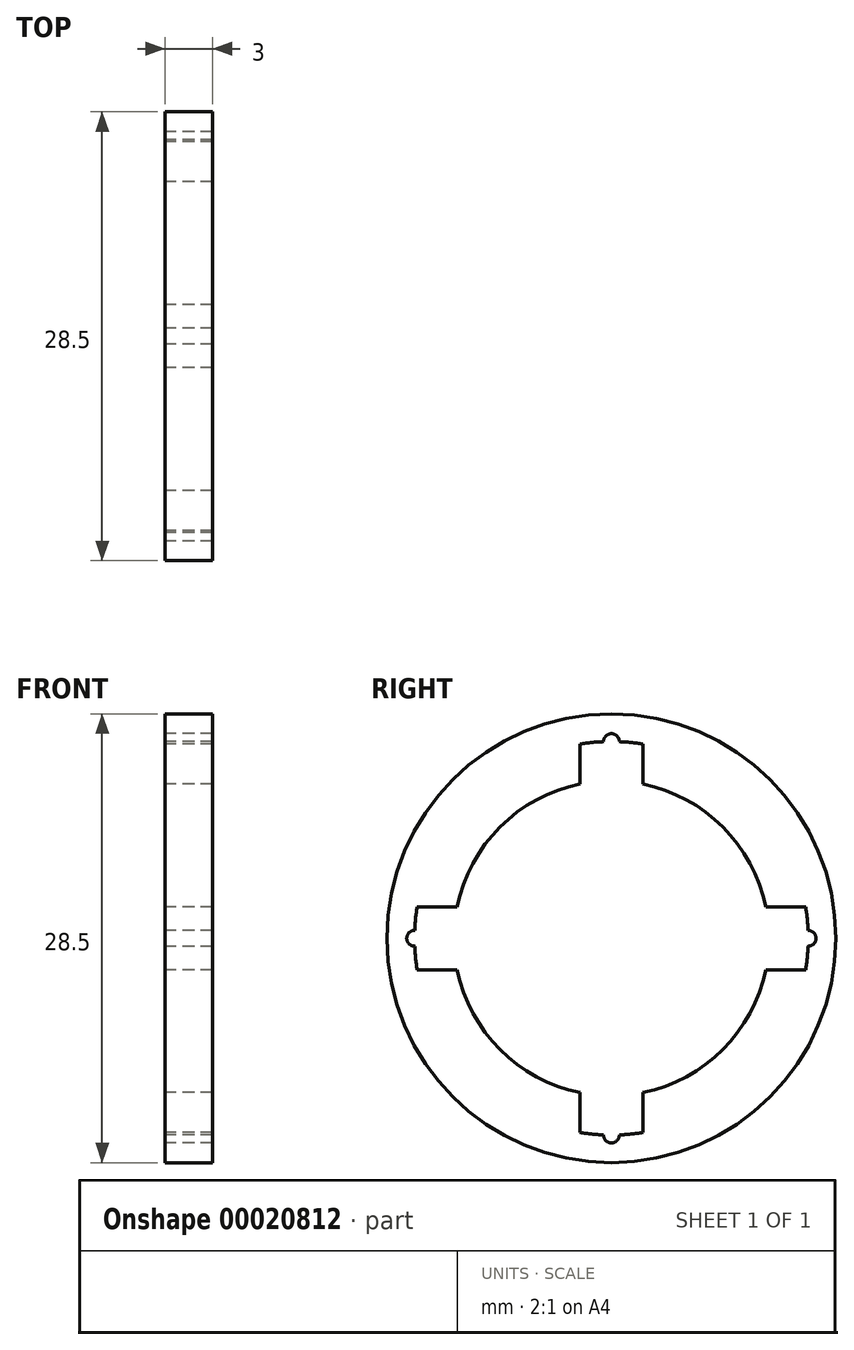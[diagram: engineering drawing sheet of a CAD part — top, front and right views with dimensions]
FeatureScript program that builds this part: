
annotation { "Feature Type Name" : "Feature", "Feature Type Description" : "" }
export const myFeature = defineFeature(function(context is Context, id is Id, definition is map)
    precondition{}
    {
        {
            var Q0;
            Q0=qCreatedBy(makeId("Right.planeOp"),FACE);
            var sketch = newSketch(context, id + "F0", { "sketchPlane" : qUnion([Q0])});
            skCircle(sketch, "E0", {"center": v(0, 0) * mm, "radius": 10 * mm});
            skCircle(sketch, "E1", {"center": v(0, 0) * mm, "radius": 12.5 * mm});
            skCircle(sketch, "E2", {"center": v(0, 0) * mm, "radius": 14.25 * mm});
            skLineSegment(sketch, "E3.rect.bottom", {"start": v(-12.34, 2) * mm, "end": v(12.34, 2) * mm});
            skLineSegment(sketch, "E3.rect.top", {"start": v(-12.34, -2) * mm, "end": v(12.34, -2) * mm});
            skLineSegment(sketch, "E3.rect.left", {"start": v(-12.34, 2) * mm, "end": v(-12.34, -2) * mm});
            skLineSegment(sketch, "E3.rect.right", {"start": v(12.34, 2) * mm, "end": v(12.34, -2) * mm});
            skLineSegment(sketch, "E4.rect.bottom", {"start": v(-2, 12.34) * mm, "end": v(2, 12.34) * mm});
            skLineSegment(sketch, "E4.rect.top", {"start": v(-2, -12.34) * mm, "end": v(2, -12.34) * mm});
            skLineSegment(sketch, "E4.rect.left", {"start": v(-2, 12.34) * mm, "end": v(-2, -12.34) * mm});
            skLineSegment(sketch, "E4.rect.right", {"start": v(2, 12.34) * mm, "end": v(2, -12.34) * mm});
            skCircle(sketch, "E5", {"center": v(-12.5, 0) * mm, "radius": 0.5 * mm});
            skCircle(sketch, "E6", {"center": v(12.5, 0) * mm, "radius": 0.5 * mm});
            skCircle(sketch, "E7", {"center": v(0, 12.5) * mm, "radius": 0.5 * mm});
            skCircle(sketch, "E8", {"center": v(0, -12.5) * mm, "radius": 0.5 * mm});
            skSolve(sketch);
        }
        {
            var Q0;
            Q0=makeQuery(id+"F0.imprint","IMPRINT",FACE,{"disambiguationData":[TD([[makeQuery(id+"F0.imprint","IMPRINT",EDGE,{"derivedFrom":sQuery(id+"F0.wireOp",EDGE,"E2")}),1.0]])]});
            var Q1;
            {var subQ0=sQuery(id+"F0.wireOp",EDGE,"E4.rect.left");var subQ1=sQuery(id+"F0.wireOp",EDGE,"E0");var subQ2=makeQuery(id+"F0.imprint","INTERSECT",VERTEX,{"disambiguationData":[OD(0.0)],"derivedFrom":[subQ1,subQ0]});Q1=makeQuery(id+"F0.imprint","IMPRINT",FACE,{"disambiguationData":[TD([[makeQuery(id+"F0.imprint","IMPRINT",EDGE,{"disambiguationData":[TD([[subQ2,-1.0]])],"derivedFrom":subQ1}),-1.0]])]});}
            var Q2;
            {var subQ1=sQuery(id+"F0.wireOp",EDGE,"E0");var subQ5=sQuery(id+"F0.wireOp",EDGE,"E3.rect.top");var subQ6=makeQuery(id+"F0.imprint","INTERSECT",VERTEX,{"disambiguationData":[OD(0.0)],"derivedFrom":[subQ1,subQ5]});Q2=makeQuery(id+"F0.imprint","IMPRINT",FACE,{"disambiguationData":[TD([[makeQuery(id+"F0.imprint","IMPRINT",EDGE,{"disambiguationData":[TD([[subQ6,-1.0]])],"derivedFrom":subQ1}),-1.0]])]});}
            var Q3;
            {var subQ0=sQuery(id+"F0.wireOp",EDGE,"E4.rect.right");var subQ1=sQuery(id+"F0.wireOp",EDGE,"E0");var subQ2=makeQuery(id+"F0.imprint","INTERSECT",VERTEX,{"disambiguationData":[OD(1.0)],"derivedFrom":[subQ1,subQ0]});Q3=makeQuery(id+"F0.imprint","IMPRINT",FACE,{"disambiguationData":[TD([[makeQuery(id+"F0.imprint","IMPRINT",EDGE,{"disambiguationData":[TD([[subQ2,-1.0]])],"derivedFrom":subQ1}),-1.0]])]});}
            var Q4;
            {var subQ0=sQuery(id+"F0.wireOp",EDGE,"E4.rect.right");var subQ1=sQuery(id+"F0.wireOp",EDGE,"E0");var subQ2=makeQuery(id+"F0.imprint","INTERSECT",VERTEX,{"disambiguationData":[OD(0.0)],"derivedFrom":[subQ1,subQ0]});Q4=makeQuery(id+"F0.imprint","IMPRINT",FACE,{"disambiguationData":[TD([[makeQuery(id+"F0.imprint","IMPRINT",EDGE,{"disambiguationData":[TD([[subQ2,1.0]])],"derivedFrom":subQ1}),-1.0]])]});}
            extrude(context, id + "F1", {"entities" : qUnion([Q0, Q1, Q2, Q3, Q4]), "depth" : 3 * mm});
        }
    });
